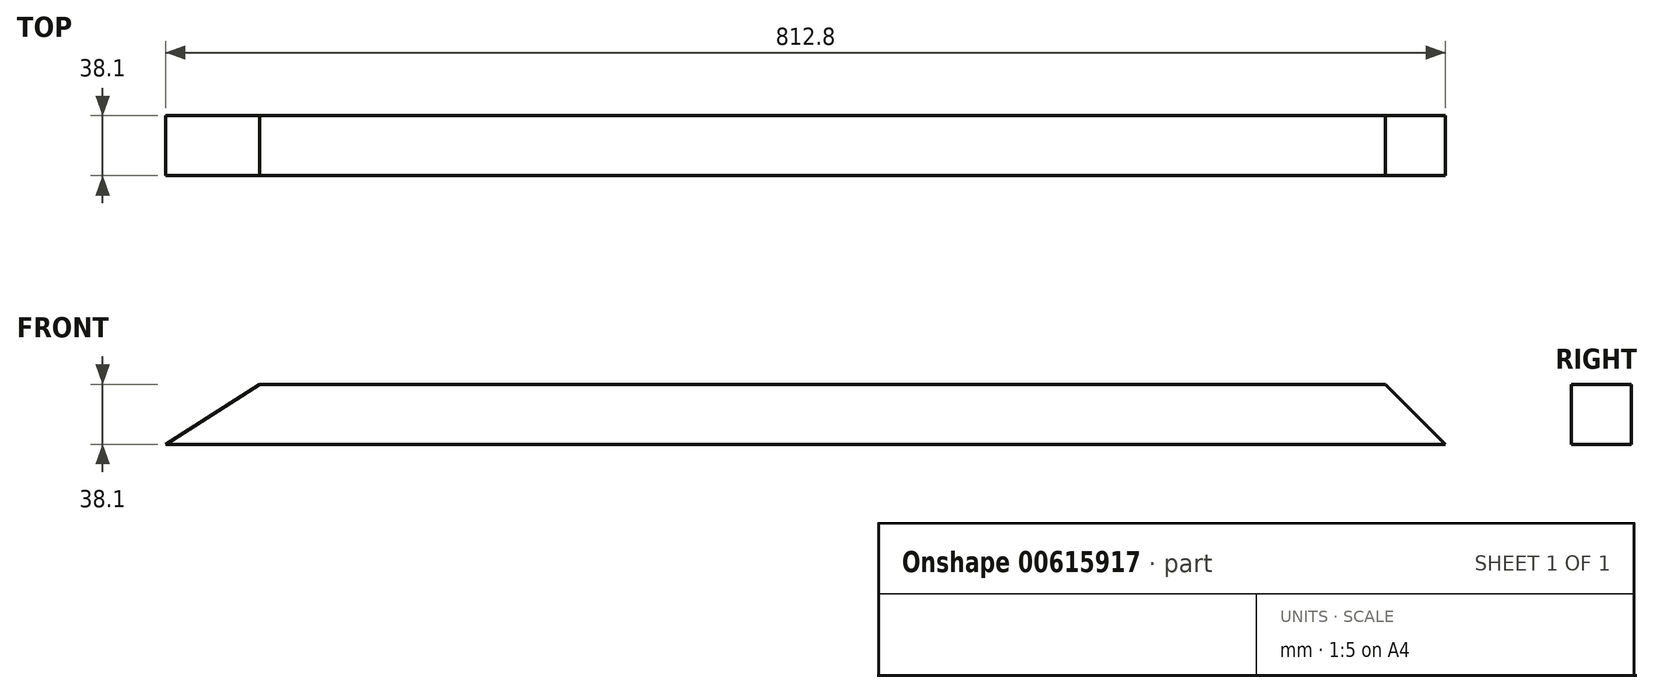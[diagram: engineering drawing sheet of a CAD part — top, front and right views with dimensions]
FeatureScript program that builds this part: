
annotation { "Feature Type Name" : "Feature", "Feature Type Description" : "" }
export const myFeature = defineFeature(function(context is Context, id is Id, definition is map)
    precondition{}
    {
        {
            var Q0;
            Q0=qCreatedBy(makeId("Front.planeOp"),FACE);
            var sketch = newSketch(context, id + "F0", { "sketchPlane" : qUnion([Q0])});
            skLineSegment(sketch, "E0.top", {"start": v(-406.4, -19.05) * mm, "end": v(406.4, -19.05) * mm});
            skLineSegment(sketch, "E0.right", {"start": v(406.4, 19.05) * mm, "end": v(406.4, -19.05) * mm});
            skPoint(sketch, "E0.middle", {"position": v(0, 0) * mm});
            skLineSegment(sketch, "E1", {"start": v(-406.4, -19.05) * mm, "end": v(-346.6, 19.05) * mm});
            skLineSegment(sketch, "E2", {"start": v(-346.6, 19.05) * mm, "end": v(406.4, 19.05) * mm});
            skSolve(sketch);
        }
        {
            var Q0;
            Q0=makeQuery(id+"F0.imprint","IMPRINT",FACE,{"disambiguationData":[TD([[makeQuery(id+"F0.imprint","IMPRINT",EDGE,{"derivedFrom":sQuery(id+"F0.wireOp",EDGE,"E0.top")}),1.0]])]});
            extrude(context, id + "F1", {"entities" : qUnion([Q0]), "endBound" : BoundingType.SYMMETRIC, "depth" : 38.1 * mm, "offsetDistance" : 25.4 * mm});
        }
        {
            var Q0;
            Q0=makeQuery(id+"F1.opExtrude","SWEPT_EDGE",EDGE,{"disambiguationData":[OSD([sQuery(id+"F0.wireOp",EDGE,"E0.right"),sQuery(id+"F0.wireOp",EDGE,"E2")])]});
            chamfer(context, id + "F2", {"entities" : qUnion([Q0]), "width" : 38.1 * mm, "tangentPropagation" : true});
        }
    });
